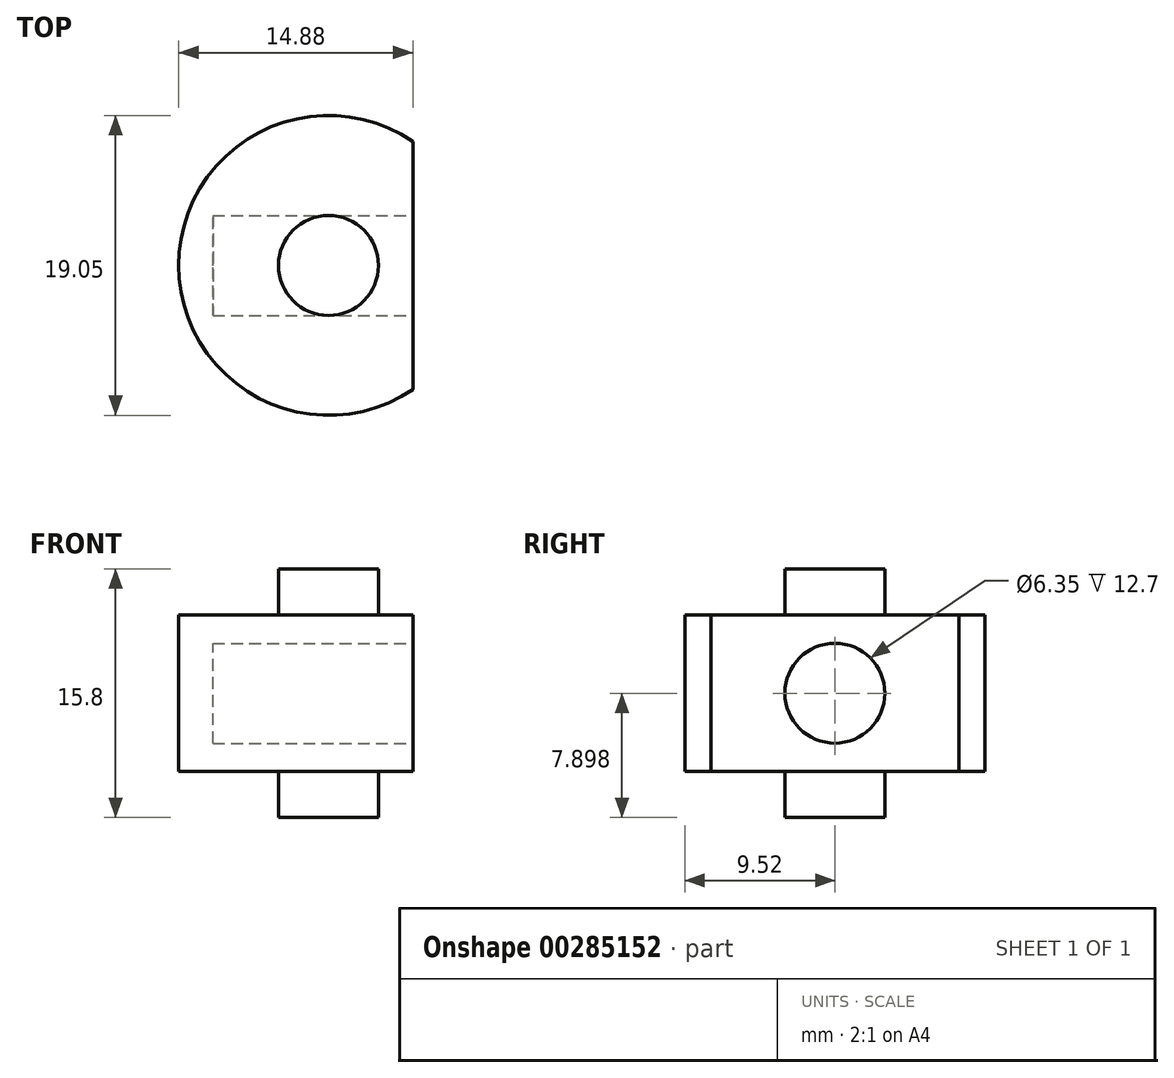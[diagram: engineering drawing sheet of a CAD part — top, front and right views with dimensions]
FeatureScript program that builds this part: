
annotation { "Feature Type Name" : "Feature", "Feature Type Description" : "" }
export const myFeature = defineFeature(function(context is Context, id is Id, definition is map)
    precondition{}
    {
        {
            var Q0;
            Q0=qCreatedBy(makeId("Top.planeOp"),FACE);
            var sketch = newSketch(context, id + "F0", { "sketchPlane" : qUnion([Q0])});
            skArc(sketch, "E0", {"start": v(5.36, 7.87) * mm, "mid": v(-9.53, 0) * mm, "end": v(5.36, -7.87) * mm});
            skLineSegment(sketch, "E1", {"start": v(5.36, -7.87) * mm, "end": v(5.36, 7.87) * mm});
            skSolve(sketch);
        }
        {
            var Q0;
            Q0 = qSketchRegion(id + "F0", true);
            extrude(context, id + "F1", {"entities" : qUnion([Q0]), "depth" : 9.96 * mm});
        }
        {
            var Q0;
            Q0=makeQuery(id+"F1.opExtrude","CAP_FACE",FACE,{"disambiguationData":[OSD([sQuery(id+"F0.wireOp",EDGE,"E0")])],"isStart":false});
            var sketch = newSketch(context, id + "F2", { "sketchPlane" : qUnion([Q0])});
            skCircle(sketch, "E2", {"center": v(0, 0) * mm, "radius": 3.18 * mm});
            skSolve(sketch);
        }
        {
            var Q0;
            Q0=makeQuery(id+"F2.imprint","IMPRINT",FACE,{"disambiguationData":[TD([[makeQuery(id+"F2.imprint","IMPRINT",EDGE,{"derivedFrom":sQuery(id+"F2.wireOp",EDGE,"E2")}),1.0]])]});
            extrude(context, id + "F3", {"entities" : qUnion([Q0]), "operationType" : NewBodyOperationType.ADD, "depth" : 2.92 * mm});
        }
        {
            var Q0;
            Q0=makeQuery(id+"F1.opExtrude","CAP_FACE",FACE,{"disambiguationData":[OSD([sQuery(id+"F0.wireOp",EDGE,"E0")])],"isStart":true});
            var sketch = newSketch(context, id + "F4", { "sketchPlane" : qUnion([Q0])});
            skCircle(sketch, "E3", {"center": v(0, 0) * mm, "radius": 3.18 * mm});
            skSolve(sketch);
        }
        {
            var Q0;
            Q0=makeQuery(id+"F4.imprint","IMPRINT",FACE,{"disambiguationData":[TD([[makeQuery(id+"F4.imprint","IMPRINT",EDGE,{"derivedFrom":sQuery(id+"F4.wireOp",EDGE,"E3")}),1.0]])]});
            extrude(context, id + "F5", {"entities" : qUnion([Q0]), "operationType" : NewBodyOperationType.ADD, "depth" : 2.92 * mm});
        }
        {
            var Q0;
            Q0=makeQuery(id+"F1.opExtrude","SWEPT_FACE",FACE,{"disambiguationData":[OSD([sQuery(id+"F0.wireOp",EDGE,"E1")])]});
            var sketch = newSketch(context, id + "F6", { "sketchPlane" : qUnion([Q0])});
            skLineSegment(sketch, "E4.0.0", {"start": v(-7.87, 0) * mm, "end": v(7.87, 0) * mm});
            skLineSegment(sketch, "E4.0.1", {"start": v(7.87, 0) * mm, "end": v(7.87, 9.96) * mm});
            skLineSegment(sketch, "E4.0.2", {"start": v(7.87, 9.96) * mm, "end": v(-7.87, 9.96) * mm});
            skLineSegment(sketch, "E4.0.3", {"start": v(-7.87, 9.96) * mm, "end": v(-7.87, 0) * mm});
            skLineSegment(sketch, "E5", {"start": v(-7.87, 9.96) * mm, "end": v(7.87, 0) * mm, "construction": true});
            skCircle(sketch, "E6", {"center": v(0, 4.98) * mm, "radius": 3.18 * mm});
            skSolve(sketch);
        }
        {
            var Q0;
            Q0=makeQuery(id+"F6.imprint","IMPRINT",FACE,{"disambiguationData":[TD([[makeQuery(id+"F6.imprint","IMPRINT",EDGE,{"derivedFrom":sQuery(id+"F6.wireOp",EDGE,"E6")}),1.0]])]});
            extrude(context, id + "F7", {"entities" : qUnion([Q0]), "operationType" : NewBodyOperationType.REMOVE, "oppositeDirection" : true, "depth" : 12.7 * mm});
        }
    });
